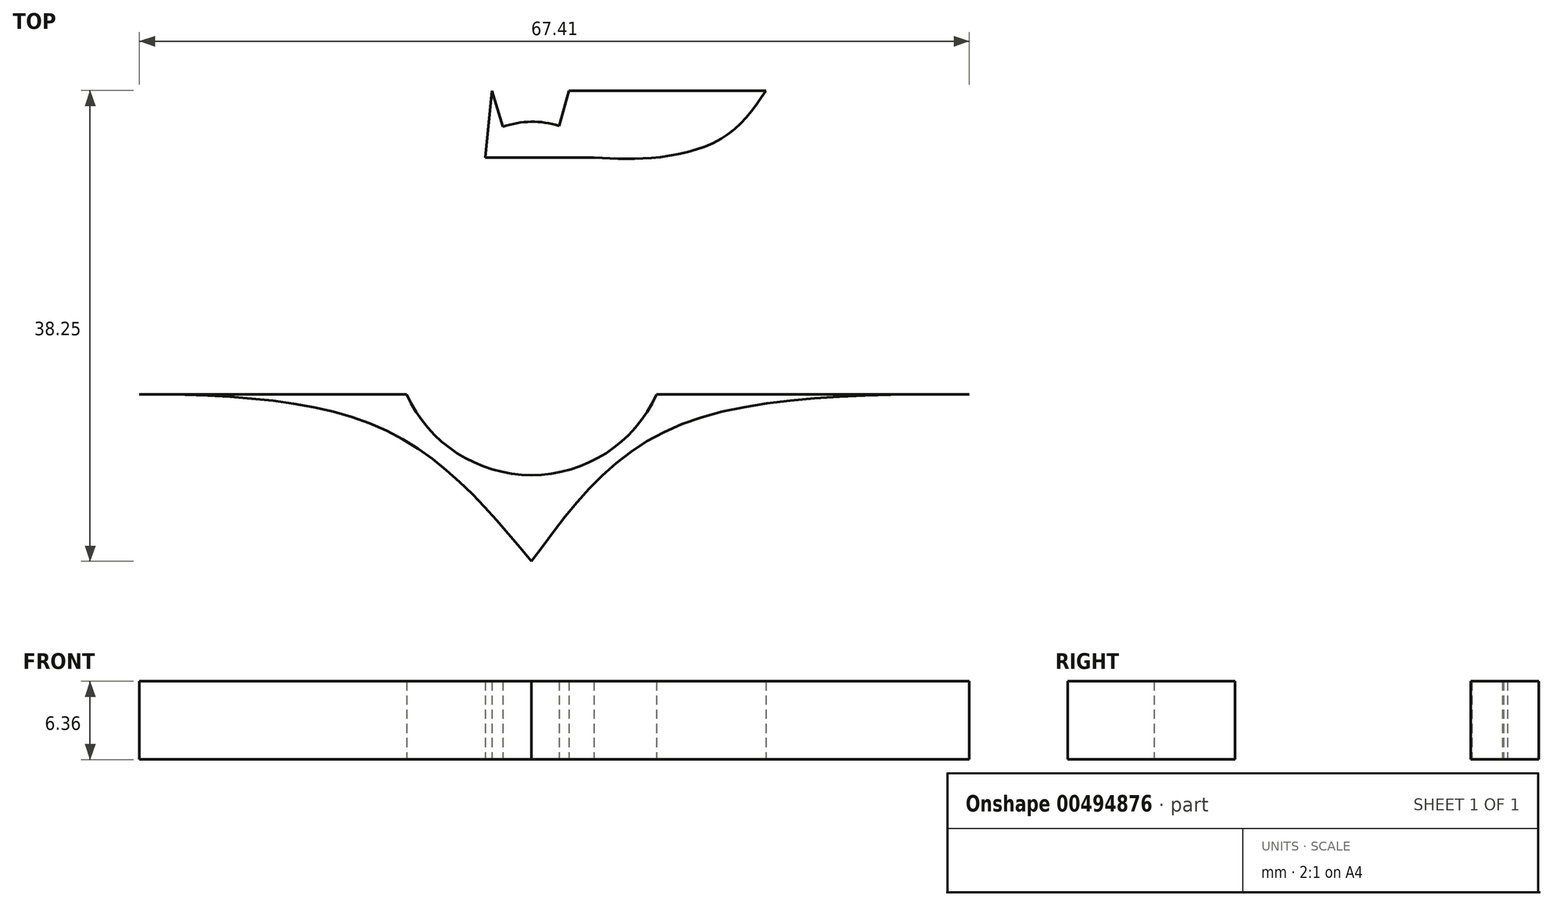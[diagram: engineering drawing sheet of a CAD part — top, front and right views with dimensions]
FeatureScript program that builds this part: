
annotation { "Feature Type Name" : "Feature", "Feature Type Description" : "" }
export const myFeature = defineFeature(function(context is Context, id is Id, definition is map)
    precondition{}
    {
        {
            var Q0;
            Q0=qCreatedBy(makeId("Top.planeOp"),FACE);
            var sketch = newSketch(context, id + "F0", { "sketchPlane" : qUnion([Q0])});
            skCircle(sketch, "E0", {"center": v(0, 0) * mm, "radius": 11.11 * mm});
            skLineSegment(sketch, "E1", {"start": v(0, 20.14) * mm, "end": v(50.8, 20.14) * mm});
            skLineSegment(sketch, "E2", {"start": v(0, 20.14) * mm, "end": v(-50.8, 20.14) * mm});
            skLineSegment(sketch, "E3", {"start": v(0, 14.7) * mm, "end": v(5.08, 14.7) * mm});
            skLineSegment(sketch, "E4", {"start": v(0, 14.7) * mm, "end": v(-5.08, 14.7) * mm});
            skLineSegment(sketch, "E5", {"start": v(0, 20.14) * mm, "end": v(-19.05, 20.14) * mm});
            skLineSegment(sketch, "E6", {"start": v(0, 20.14) * mm, "end": v(19.05, 20.14) * mm});
            skFitSpline(sketch, "E7", {"points": [v(-19.05, 20.14) * mm, v(-14.15, 16.6) * mm, v(-9.25, 14.7) * mm, v(-5.08, 14.7) * mm], "startDerivative": vector(13.22, -10.5) * mm, "endDerivative": vector(13.7, 0) * mm});
            skFitSpline(sketch, "E8", {"points": [v(19.05, 20.14) * mm, v(15.68, 16.4) * mm, v(10.04, 14.7) * mm, v(5.08, 14.7) * mm], "startDerivative": vector(-8.86, -12.89) * mm, "endDerivative": vector(-14.8, 0.8) * mm});
            skLineSegment(sketch, "E9", {"start": v(-3.77, 14.7) * mm, "end": v(-3.23, 20.14) * mm});
            skLineSegment(sketch, "E10", {"start": v(-3.23, 20.14) * mm, "end": v(-2.32, 17.2) * mm});
            skLineSegment(sketch, "E11", {"start": v(3.56, 14.7) * mm, "end": v(3.02, 20.14) * mm});
            skLineSegment(sketch, "E12", {"start": v(3.02, 20.14) * mm, "end": v(2.23, 17.28) * mm});
            skArc(sketch, "E13", {"start": v(2.23, 17.28) * mm, "mid": v(-0.05, 17.6) * mm, "end": v(-2.32, 17.2) * mm});
            skLineSegment(sketch, "E14", {"start": v(0, -4.54) * mm, "end": v(35.56, -4.54) * mm});
            skLineSegment(sketch, "E15", {"start": v(0, -4.54) * mm, "end": v(-35.56, -4.54) * mm});
            skFitSpline(sketch, "E16", {"points": [v(-35.56, -4.54) * mm, v(-35.56, 9.42) * mm, v(-50.8, 20.14) * mm], "startDerivative": vector(6.6, 32.43) * mm, "endDerivative": vector(-36.05, 17.3) * mm});
            skFitSpline(sketch, "E17", {"points": [v(35.56, -4.54) * mm, v(35.56, 9.89) * mm, v(50.8, 20.14) * mm], "startDerivative": vector(-6.75, 33.38) * mm, "endDerivative": vector(36.37, 16.33) * mm});
            skFitSpline(sketch, "E18", {"points": [v(-35.56, -4.54) * mm, v(-12.27, -7.27) * mm, v(0, -18.11) * mm], "startDerivative": vector(47.06, 0.1) * mm, "endDerivative": vector(23.35, -28.1) * mm});
            skFitSpline(sketch, "E19", {"points": [v(35.56, -4.54) * mm, v(10.84, -7.56) * mm, v(0, -18.11) * mm], "startDerivative": vector(-49.4, -0.1) * mm, "endDerivative": vector(-20.53, -28.2) * mm});
            skSolve(sketch);
        }
        {
            var Q0;
            {var subQ4=sQuery(id+"F0.wireOp",EDGE,"E9");Q0=makeQuery(id+"F0.imprint","IMPRINT",FACE,{"disambiguationData":[TD([[makeQuery(id+"F0.imprint","IMPRINT",EDGE,{"derivedFrom":subQ4}),-1.0]])]});}
            extrude(context, id + "F1", {"entities" : qUnion([Q0]), "endBound" : BoundingType.SYMMETRIC, "depth" : 6.35 * mm});
        }
        {
            var Q0;
            Q0=makeQuery(id+"F0.imprint","IMPRINT",FACE,{"disambiguationData":[TD([[makeQuery(id+"F0.imprint","IMPRINT",EDGE,{"derivedFrom":sQuery(id+"F0.wireOp",EDGE,"E1")}),-1.0]])]});
            extrude(context, id + "F2", {"entities" : qUnion([Q0]), "operationType" : NewBodyOperationType.ADD, "endBound" : BoundingType.SYMMETRIC, "depth" : 6.35 * mm});
        }
        {
            var Q0;
            {var subQ0=sQuery(id+"F0.wireOp",EDGE,"E19");Q0=makeQuery(id+"F0.imprint","IMPRINT",FACE,{"disambiguationData":[TD([[makeQuery(id+"F0.imprint","IMPRINT",EDGE,{"derivedFrom":subQ0}),-1.0]])]});}
            extrude(context, id + "F3", {"entities" : qUnion([Q0]), "operationType" : NewBodyOperationType.ADD, "endBound" : BoundingType.SYMMETRIC, "depth" : 6.35 * mm});
        }
    });
